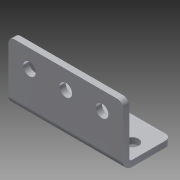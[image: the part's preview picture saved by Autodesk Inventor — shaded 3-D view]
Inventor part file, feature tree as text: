
AUTODESK INVENTOR PART (.ipt)
format: ipt  version: 2013 (Build 170138000, 138)  size: 176,128 bytes
history: native  units: in
note: dims shown in document units (in); Inventor stores cm internally (conversion verified against a paired STEP export)
features: sheet_metal_op x4, other x4, sketch x3, chamfer x1
ambient origin geometry x8: Origin, YZ Plane, XZ Plane, XY Plane, X Axis, Y Axis, Z Axis, Center Point
bodies: Solid1 (feature_tree)
feature tree (12):
  sheet_metal_op  "Face1"
  sheet_metal_op  "Flange1"
  chamfer  "Corner Round1"
  sketch  "Sketch1"  dims[d0=2.375in]
  other  "Plate1"
  sketch  "Sketch2"  dims[d1=1.0in]
  other  "Plate2"
  sheet_metal_op  "Bend1"
  sheet_metal_op  "Corner1"
  sketch  "Sketch3"  dims[d2=0.26in d3=1.75in d4=0.125in d5=0.125in d6=0.0625in d7=0.25in d8=0.125in d9=1.25in d10=90.0deg d11=0.05in d12=0.5in d13=0.125in d14=0.125in d15=1.5in d17=0.26in d19=0.875in d20=0.125in d21=0.0in d22=0.125in d23=0.3125in]
  other  "Cut1"
  other  "Definition1"
